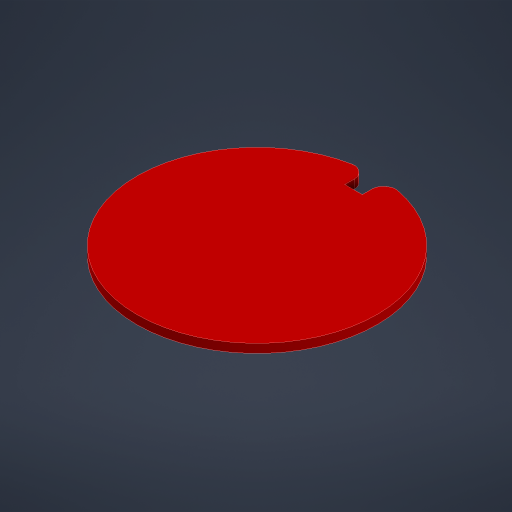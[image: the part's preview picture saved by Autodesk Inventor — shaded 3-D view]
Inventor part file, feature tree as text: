
AUTODESK INVENTOR PART (.ipt)
format: ipt  version: 2023.4 (Build 274418000, 418)  size: 239,104 bytes
history: native  units: mm
features: sketch x2, plane x2, extrude x2, reference x2, other x2, projected_geometry x1
ambient origin geometry x8: Origin, YZ Plane, XZ Plane, XY Plane, X Axis, Y Axis, Z Axis, Center Point
bodies: Solid1 (feature_tree)
feature tree (11):
  sketch  "Sketch1"  dims[d2=1.0mm d3=0.0mm d7=1.0mm d8=0.0mm]
  plane  "Work Plane1"
  extrude  "Extrusion1"  Depth=1.0mm TaperAngle=0.0deg
  plane  "Work Plane2"
  extrude  "Extrusion2"  Depth=1.125mm
  sketch  "Sketch2"  dims[d21=0.05mm d22=2.5mm d23=0.05mm d24=0.9375mm d25=9.75mm d26=3.75mm d27=1.0mm d28=2.0mm d29=45.0deg d30=1.125mm]
  projected_geometry  "Projected Loop2"
  reference  "Reference12"
  reference  "Reference13"
  other  "XYZ Stage V5.iam"
  other  "Z Stage Body V5:1"
